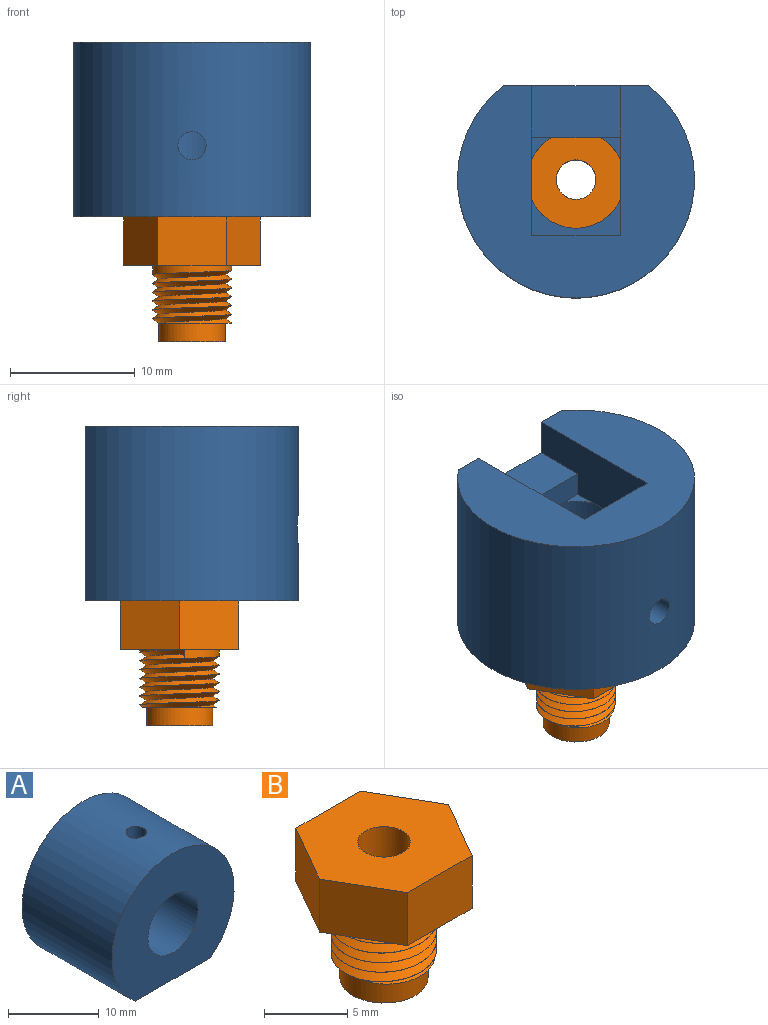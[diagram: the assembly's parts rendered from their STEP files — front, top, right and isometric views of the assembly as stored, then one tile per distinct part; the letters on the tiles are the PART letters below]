
ASSEMBLY  parts=2 mates=2
PART A: 17 faces, bbox 19x14x17 mm
  f0: cylinder r=9.5mm len=19mm, axis (0,-1,0), area 655.9mm2, adj f4,f9,f10,f16
  f1: cylinder r=3.9mm len=9mm, axis (0,-1,0), area 216.7mm2, adj f2,f3,f9,f11,f13,f14,f15,f16
  f2: plane 3.25x0.35mm, normal (0,-1,0), area 0.8mm2, adj f1,f6
  f3: plane 3.25x0.35mm, normal (0,-1,0), area 0.8mm2, adj f1,f8
  f4: plane 19x17mm, normal (0,1,0), area 182.4mm2, adj f0,f6,f7,f8,f10
  f5: plane 7.1x2mm, normal (0,0,1), area 14.2mm2, adj f6,f8,f11,f12,f13,f14
  f6: plane 12x5mm, normal (1,0,0), area 51.7mm2, adj f2,f4,f5,f7,f10,f12,f14,f15
  f7: plane 7.1x5mm, normal (0,0,-1), area 35.5mm2, adj f4,f6,f8,f15
  f8: plane 12x5mm, normal (-1,0,0), area 51.7mm2, adj f3,f4,f5,f7,f10,f12,f13,f15
  f9: plane 19x17mm, normal (0,-1,0), area 219.8mm2, adj f0,f1,f10
  f10: plane 14x11.66mm, normal (0,0,-1), area 142mm2, adj f0,f4,f6,f8,f9,f12
  f11: plane 4.05x0.57mm, normal (0,-1,0), area 1.5mm2, adj f1,f5
  f12: plane 7.1x4.16mm, normal (0,1,0), area 29.6mm2, adj f5,f6,f8,f10
  f13: plane 1.72x1.53mm, normal (0,1,0), area 1mm2, adj f1,f5,f8
  f14: plane 1.72x1.53mm, normal (0,1,0), area 1mm2, adj f1,f5,f6
  f15: plane 7.1x2.88mm, normal (0,1,0), area 8.8mm2, adj f1,f6,f7,f8
  f16: cylinder r=1.13mm len=5.76mm, axis (0,0,1), area 40.1mm2, adj f0,f1
PART B: 18 faces, bbox 11.4x9.9x10.4 mm
  f0: cylinder r=3.17mm len=6.35mm, axis (0,0,1), area 14.5mm2, adj f3,f13,f15,f16,f17
  f1: cylinder r=1.59mm len=8mm, axis (0,0,-1), area 79.8mm2, adj f4,f12
  f2: plane 5.3x5.3mm, normal (0,0,-1), area 4.7mm2, adj f11,f14
  f3: plane 10.97x9.5mm, normal (0,0,-1), area 46.5mm2, adj f0,f5,f6,f7,f8,f9,f10
  f4: plane 10.97x9.5mm, normal (0,0,1), area 70.2mm2, adj f1,f5,f6,f7,f8,f9,f10
  f5: plane 4.75x3.9mm, normal (-0.87,0.5,0), area 21.4mm2, adj f3,f4,f6,f10
  f6: plane 4.75x3.9mm, normal (-0.87,-0.5,0), area 21.4mm2, adj f3,f4,f5,f7
  f7: plane 5.48x3.9mm, normal (0,-1,0), area 21.4mm2, adj f3,f4,f6,f8
  f8: plane 4.75x3.9mm, normal (0.87,-0.5,0), area 21.4mm2, adj f3,f4,f7,f9
  f9: plane 4.75x3.9mm, normal (0.87,0.5,0), area 21.4mm2, adj f3,f4,f8,f10
  f10: plane 5.48x3.9mm, normal (0,1,0), area 21.4mm2, adj f3,f4,f5,f9
  f11: cylinder r=2.35mm len=4.7mm, axis (0,0,-1), area 29.5mm2, adj f2,f12
  f12: plane 4.7x4.7mm, normal (0,0,-1), area 9.4mm2, adj f1,f11
  f13: plane 6.3x6.29mm, normal (0,0,-1), area 4.9mm2, adj f0,f14,f16,f17
  f14: cylinder r=2.65mm len=5.3mm, axis (0,0,-1), area 25mm2, adj f2,f13
  f15: plane 0.7x0.5mm, normal (-0.13,0.99,0), area 0.2mm2, adj f0,f16,f17
  f16: bspline ~7.33x6.35mm, area 71mm2, adj f0,f13,f15,f17
  f17: bspline ~6.35x6.35mm, area 64.2mm2, adj f0,f13,f15,f16
PLACE A rot(axis=(1,0,0),90deg) t=(-11.62,-9.23,0.08)mm
PLACE B t=(-6.14,-9.23,0.08)mm
MATE cylindrical B.f0 <-> A.f1  axis (0,0,-1) through (-11.62,-9.23,0.08)mm
MATE parallel A.f9 <-> B.f0  axis (0,0,-1) through (-11.62,-9.83,0.08)mm
